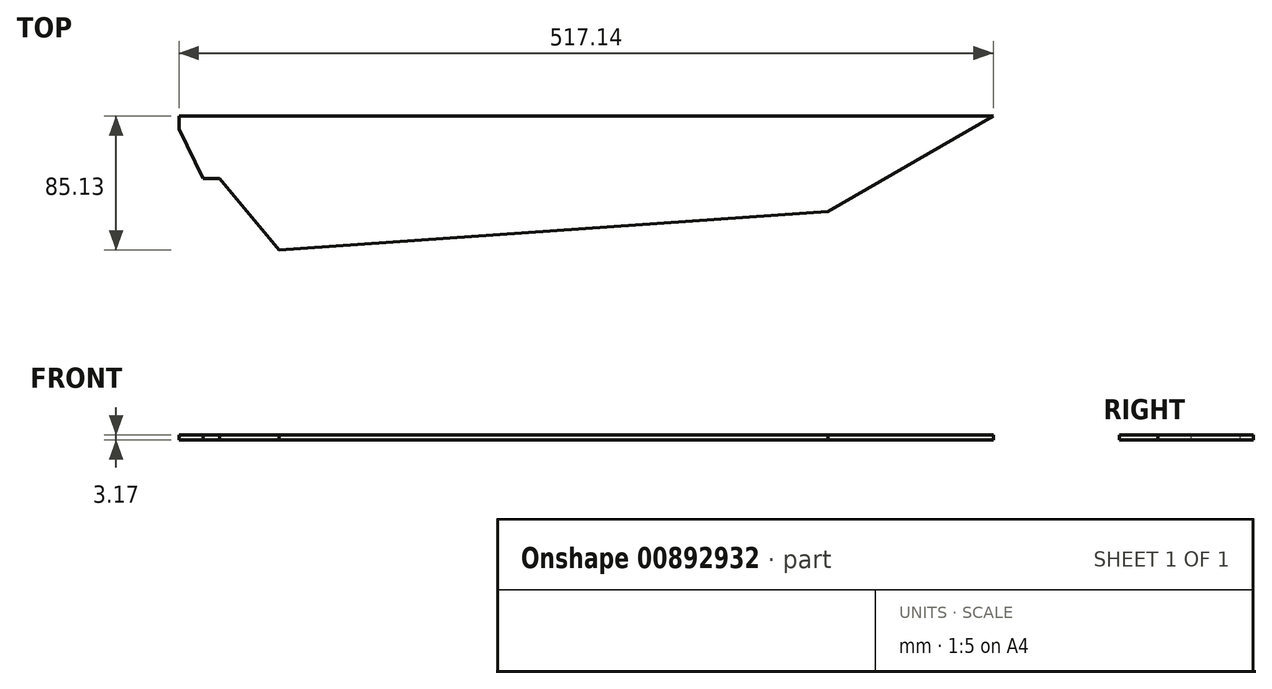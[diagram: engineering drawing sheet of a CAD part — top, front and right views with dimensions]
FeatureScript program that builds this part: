
annotation { "Feature Type Name" : "Feature", "Feature Type Description" : "" }
export const myFeature = defineFeature(function(context is Context, id is Id, definition is map)
    precondition{}
    {
        {
            var Q0;
            Q0=qCreatedBy(makeId("Top.planeOp"),FACE);
            var sketch = newSketch(context, id + "F0", { "sketchPlane" : qUnion([Q0])});
            skLineSegment(sketch, "E0", {"start": v(478.92, 47.23) * mm, "end": v(478.92, -917.97) * mm, "construction": true});
            skLineSegment(sketch, "E1", {"start": v(478.92, -917.97) * mm, "end": v(390.02, -917.97) * mm, "construction": true});
            skLineSegment(sketch, "E2", {"start": v(-54.63, -3.84) * mm, "end": v(390.02, -917.97) * mm, "construction": true});
            skLineSegment(sketch, "E3", {"start": v(-79.5, 47.23) * mm, "end": v(-79.5, 86.91) * mm});
            skCircle(sketch, "E4", {"center": v(-38.37, 20.63) * mm, "radius": 22.23 * mm});
            skLineSegment(sketch, "E5.0", {"start": v(478.92, 86.91) * mm, "end": v(-79.5, 86.91) * mm});
            skLineSegment(sketch, "E6", {"start": v(-79.5, 47.23) * mm, "end": v(-54.63, -3.84) * mm});
            skLineSegment(sketch, "E7", {"start": v(-79.5, 47.23) * mm, "end": v(410.18, 47.23) * mm});
            skLineSegment(sketch, "E8", {"start": v(478.92, 86.91) * mm, "end": v(478.92, 47.23) * mm});
            skLineSegment(sketch, "E9", {"start": v(-54.63, -3.84) * mm, "end": v(373.86, 26.26) * mm});
            skCircle(sketch, "E10", {"center": v(-38.37, 20.63) * mm, "radius": 6.35 * mm});
            skLineSegment(sketch, "E11", {"start": v(478.92, 86.91) * mm, "end": v(373.86, 26.26) * mm});
            skLineSegment(sketch, "E12", {"start": v(-38.22, 78.5) * mm, "end": v(0, 0) * mm});
            skLineSegment(sketch, "E13", {"start": v(-38.22, 78.5) * mm, "end": v(-38.22, 86.91) * mm});
            skLineSegment(sketch, "E14", {"start": v(0, 0) * mm, "end": v(25.34, 1.78) * mm});
            skLineSegment(sketch, "E15", {"start": v(25.34, 1.78) * mm, "end": v(-38.22, 78.5) * mm});
            skSolve(sketch);
        }
        {
            var Q0;
            {var subQ0=sQuery(id+"F0.wireOp",EDGE,"E13");Q0=makeQuery(id+"F0.imprint","IMPRINT",FACE,{"disambiguationData":[TD([[makeQuery(id+"F0.imprint","IMPRINT",EDGE,{"derivedFrom":subQ0}),-1.0]])]});}
            var Q1;
            {var subQ0=sQuery(id+"F0.wireOp",EDGE,"E12");var subQ1=sQuery(id+"F0.wireOp",EDGE,"E7");var subQ2=makeQuery(id+"F0.imprint","INTERSECT",VERTEX,{"derivedFrom":[subQ1,subQ0]});Q1=makeQuery(id+"F0.imprint","IMPRINT",FACE,{"disambiguationData":[TD([[makeQuery(id+"F0.imprint","IMPRINT",EDGE,{"disambiguationData":[TD([[subQ2,-1.0]])],"derivedFrom":subQ1}),1.0]])]});}
            var Q2;
            {var subQ5=sQuery(id+"F0.wireOp",EDGE,"E14");Q2=makeQuery(id+"F0.imprint","IMPRINT",FACE,{"disambiguationData":[TD([[makeQuery(id+"F0.imprint","IMPRINT",EDGE,{"derivedFrom":subQ5}),1.0]])]});}
            var Q3;
            {var subQ0=sQuery(id+"F0.wireOp",EDGE,"E11");var subQ1=sQuery(id+"F0.wireOp",EDGE,"E7");var subQ2=makeQuery(id+"F0.imprint","INTERSECT",VERTEX,{"derivedFrom":[subQ1,subQ0]});Q3=makeQuery(id+"F0.imprint","IMPRINT",FACE,{"disambiguationData":[TD([[makeQuery(id+"F0.imprint","IMPRINT",EDGE,{"disambiguationData":[TD([[subQ2,1.0]])],"derivedFrom":subQ1}),-1.0]])]});}
            extrude(context, id + "F1", {"entities" : qUnion([Q0, Q1, Q2, Q3]), "depth" : 3.17 * mm, "offsetDistance" : 25.4 * mm});
        }
    });
